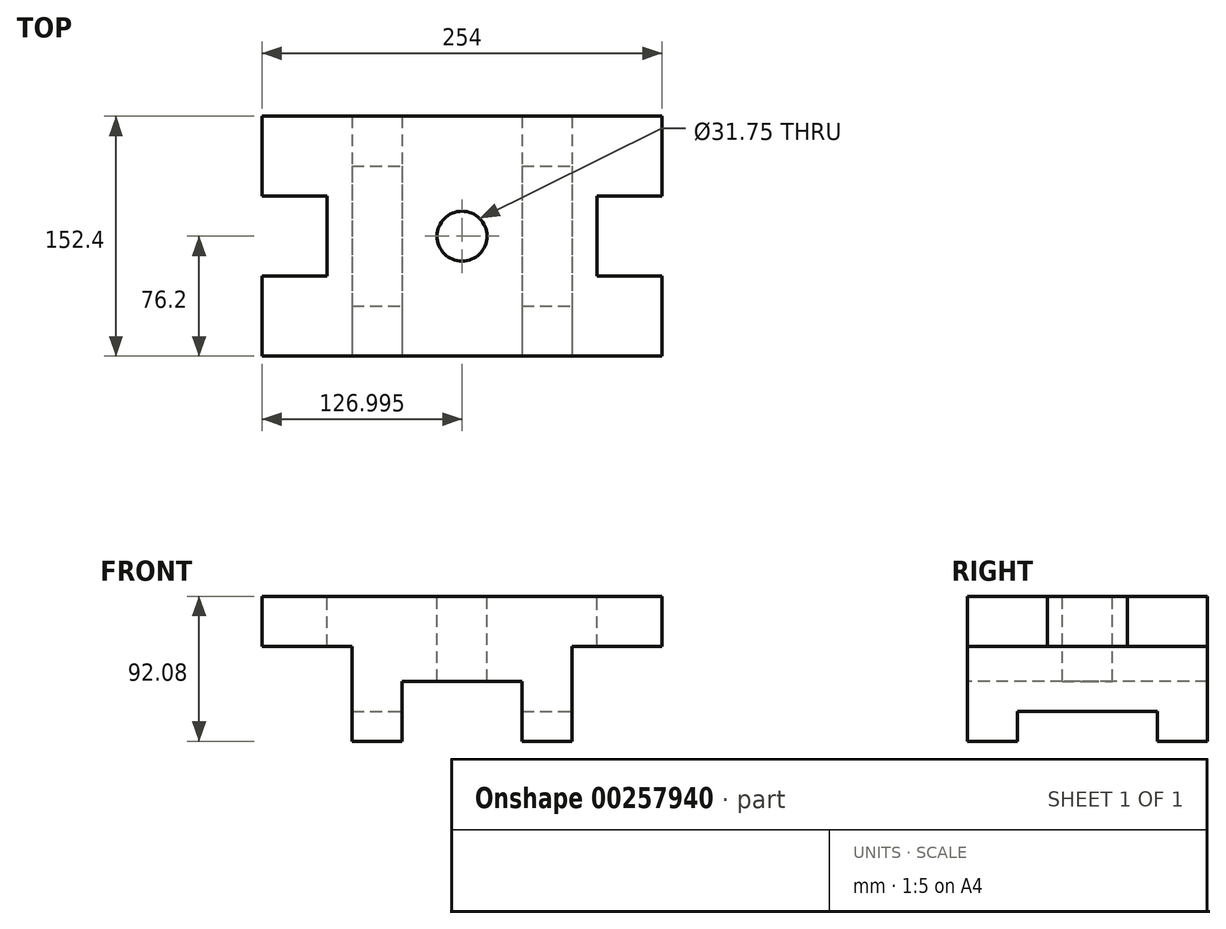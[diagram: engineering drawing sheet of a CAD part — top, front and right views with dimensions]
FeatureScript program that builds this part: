
annotation { "Feature Type Name" : "Feature", "Feature Type Description" : "" }
export const myFeature = defineFeature(function(context is Context, id is Id, definition is map)
    precondition{}
    {
        {
            var Q0;
            Q0=qCreatedBy(makeId("Top.planeOp"),FACE);
            var sketch = newSketch(context, id + "F0", { "sketchPlane" : qUnion([Q0])});
            skLineSegment(sketch, "E0.bottom", {"start": v(-152.98, 76.2) * mm, "end": v(101.02, 76.2) * mm});
            skLineSegment(sketch, "E0.top", {"start": v(-152.98, -76.2) * mm, "end": v(101.02, -76.2) * mm});
            skLineSegment(sketch, "E0.left", {"start": v(-152.98, 76.2) * mm, "end": v(-152.98, 25.4) * mm});
            skLineSegment(sketch, "E0.right", {"start": v(101.02, 76.2) * mm, "end": v(101.02, 25.4) * mm});
            skLineSegment(sketch, "E1", {"start": v(-152.98, 25.4) * mm, "end": v(-111.7, 25.4) * mm});
            skLineSegment(sketch, "E2", {"start": v(-111.7, 25.4) * mm, "end": v(-111.7, -25.4) * mm});
            skLineSegment(sketch, "E3", {"start": v(-152.98, -25.4) * mm, "end": v(-111.7, -25.4) * mm});
            skLineSegment(sketch, "E4", {"start": v(59.74, 25.4) * mm, "end": v(59.74, -25.4) * mm});
            skLineSegment(sketch, "E5", {"start": v(59.74, -25.4) * mm, "end": v(101.02, -25.4) * mm});
            skLineSegment(sketch, "E6", {"start": v(59.74, 25.4) * mm, "end": v(101.02, 25.4) * mm});
            skLineSegment(sketch, "E7", {"start": v(-95.83, 76.2) * mm, "end": v(-95.83, -76.2) * mm});
            skLineSegment(sketch, "E8", {"start": v(43.87, 76.2) * mm, "end": v(43.87, -76.2) * mm});
            skLineSegment(sketch, "E9", {"start": v(-64.08, 76.2) * mm, "end": v(-64.08, -76.2) * mm});
            skLineSegment(sketch, "E10", {"start": v(-95.83, -44.45) * mm, "end": v(-64.08, -44.45) * mm});
            skLineSegment(sketch, "E11", {"start": v(-95.83, 44.45) * mm, "end": v(-64.08, 44.45) * mm});
            skLineSegment(sketch, "E12", {"start": v(12.12, 76.2) * mm, "end": v(12.12, -76.2) * mm});
            skLineSegment(sketch, "E13", {"start": v(12.12, 44.45) * mm, "end": v(43.87, 44.45) * mm});
            skLineSegment(sketch, "E14", {"start": v(12.12, -44.45) * mm, "end": v(43.87, -44.45) * mm});
            skCircle(sketch, "E15", {"center": v(-25.98, 0) * mm, "radius": 15.88 * mm});
            skLineSegment(sketch, "E16.trimOffspring", {"start": v(-152.98, -25.4) * mm, "end": v(-152.98, -76.2) * mm});
            skLineSegment(sketch, "E17.trimOffspring", {"start": v(101.02, -25.4) * mm, "end": v(101.02, -76.2) * mm});
            skSolve(sketch);
        }
        {
            var Q0;
            Q0=makeQuery(id+"F0.imprint","IMPRINT",FACE,{"disambiguationData":[TD([[makeQuery(id+"F0.imprint","IMPRINT",EDGE,{"derivedFrom":sQuery(id+"F0.wireOp",EDGE,"E15")}),-1.0]])]});
            var Q1;
            {var subQ5=sQuery(id+"F0.wireOp",EDGE,"E10");Q1=makeQuery(id+"F0.imprint","IMPRINT",FACE,{"disambiguationData":[TD([[makeQuery(id+"F0.imprint","IMPRINT",EDGE,{"derivedFrom":subQ5}),-1.0]])]});}
            var Q2;
            {var subQ0=sQuery(id+"F0.wireOp",EDGE,"E10");Q2=makeQuery(id+"F0.imprint","IMPRINT",FACE,{"disambiguationData":[TD([[makeQuery(id+"F0.imprint","IMPRINT",EDGE,{"derivedFrom":subQ0}),1.0]])]});}
            var Q3;
            {var subQ5=sQuery(id+"F0.wireOp",EDGE,"E11");Q3=makeQuery(id+"F0.imprint","IMPRINT",FACE,{"disambiguationData":[TD([[makeQuery(id+"F0.imprint","IMPRINT",EDGE,{"derivedFrom":subQ5}),1.0]])]});}
            var Q4;
            {var subQ5=sQuery(id+"F0.wireOp",EDGE,"E13");Q4=makeQuery(id+"F0.imprint","IMPRINT",FACE,{"disambiguationData":[TD([[makeQuery(id+"F0.imprint","IMPRINT",EDGE,{"derivedFrom":subQ5}),1.0]])]});}
            var Q5;
            {var subQ0=sQuery(id+"F0.wireOp",EDGE,"E13");Q5=makeQuery(id+"F0.imprint","IMPRINT",FACE,{"disambiguationData":[TD([[makeQuery(id+"F0.imprint","IMPRINT",EDGE,{"derivedFrom":subQ0}),-1.0]])]});}
            var Q6;
            {var subQ5=sQuery(id+"F0.wireOp",EDGE,"E14");Q6=makeQuery(id+"F0.imprint","IMPRINT",FACE,{"disambiguationData":[TD([[makeQuery(id+"F0.imprint","IMPRINT",EDGE,{"derivedFrom":subQ5}),-1.0]])]});}
            extrude(context, id + "F1", {"entities" : qUnion([Q0, Q1, Q2, Q3, Q4, Q5, Q6]), "oppositeDirection" : true, "depth" : 53.97 * mm});
        }
        {
            var Q0;
            {var subQ4=sQuery(id+"F0.wireOp",EDGE,"E0.left");Q0=makeQuery(id+"F0.imprint","IMPRINT",FACE,{"disambiguationData":[TD([[makeQuery(id+"F0.imprint","IMPRINT",EDGE,{"derivedFrom":subQ4}),1.0]])]});}
            var Q1;
            {var subQ0=sQuery(id+"F0.wireOp",EDGE,"E0.right");Q1=makeQuery(id+"F0.imprint","IMPRINT",FACE,{"disambiguationData":[TD([[makeQuery(id+"F0.imprint","IMPRINT",EDGE,{"derivedFrom":subQ0}),-1.0]])]});}
            extrude(context, id + "F2", {"entities" : qUnion([Q0, Q1]), "operationType" : NewBodyOperationType.ADD, "oppositeDirection" : true, "depth" : 31.75 * mm});
        }
        {
            var Q0;
            {var subQ0=sQuery(id+"F0.wireOp",EDGE,"E13");Q0=makeQuery(id+"F0.imprint","IMPRINT",FACE,{"disambiguationData":[TD([[makeQuery(id+"F0.imprint","IMPRINT",EDGE,{"derivedFrom":subQ0}),-1.0]])]});}
            var Q1;
            {var subQ0=sQuery(id+"F0.wireOp",EDGE,"E10");Q1=makeQuery(id+"F0.imprint","IMPRINT",FACE,{"disambiguationData":[TD([[makeQuery(id+"F0.imprint","IMPRINT",EDGE,{"derivedFrom":subQ0}),1.0]])]});}
            extrude(context, id + "F3", {"entities" : qUnion([Q0, Q1]), "operationType" : NewBodyOperationType.ADD, "oppositeDirection" : true, "depth" : 73.02 * mm});
        }
        {
            var Q0;
            {var subQ5=sQuery(id+"F0.wireOp",EDGE,"E14");Q0=makeQuery(id+"F0.imprint","IMPRINT",FACE,{"disambiguationData":[TD([[makeQuery(id+"F0.imprint","IMPRINT",EDGE,{"derivedFrom":subQ5}),-1.0]])]});}
            var Q1;
            {var subQ5=sQuery(id+"F0.wireOp",EDGE,"E10");Q1=makeQuery(id+"F0.imprint","IMPRINT",FACE,{"disambiguationData":[TD([[makeQuery(id+"F0.imprint","IMPRINT",EDGE,{"derivedFrom":subQ5}),-1.0]])]});}
            var Q2;
            {var subQ5=sQuery(id+"F0.wireOp",EDGE,"E13");Q2=makeQuery(id+"F0.imprint","IMPRINT",FACE,{"disambiguationData":[TD([[makeQuery(id+"F0.imprint","IMPRINT",EDGE,{"derivedFrom":subQ5}),1.0]])]});}
            var Q3;
            {var subQ5=sQuery(id+"F0.wireOp",EDGE,"E11");Q3=makeQuery(id+"F0.imprint","IMPRINT",FACE,{"disambiguationData":[TD([[makeQuery(id+"F0.imprint","IMPRINT",EDGE,{"derivedFrom":subQ5}),1.0]])]});}
            extrude(context, id + "F4", {"entities" : qUnion([Q0, Q1, Q2, Q3]), "operationType" : NewBodyOperationType.ADD, "oppositeDirection" : true, "depth" : 92.07 * mm});
        }
    });
